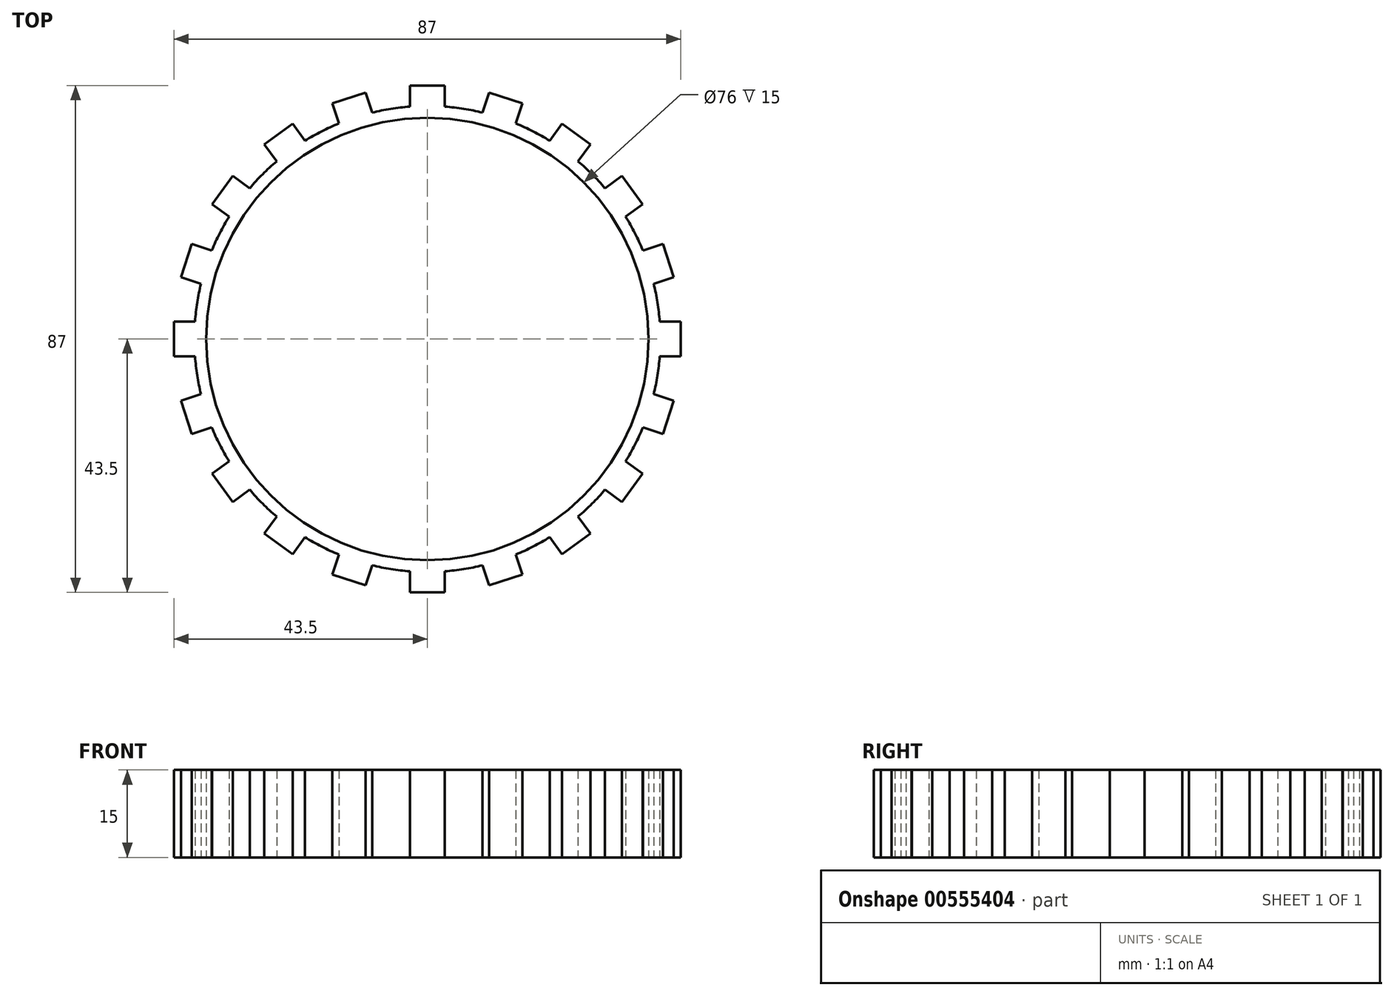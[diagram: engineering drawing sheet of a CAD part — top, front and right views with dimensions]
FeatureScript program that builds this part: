
annotation { "Feature Type Name" : "Feature", "Feature Type Description" : "" }
export const myFeature = defineFeature(function(context is Context, id is Id, definition is map)
    precondition{}
    {
        {
            var Q0;
            Q0=qCreatedBy(makeId("Top.planeOp"),FACE);
            var sketch = newSketch(context, id + "F0", { "sketchPlane" : qUnion([Q0])});
            skCircle(sketch, "E0", {"center": v(0, 0) * mm, "radius": 40 * mm});
            skCircle(sketch, "E1.0", {"center": v(0, 0) * mm, "radius": 38 * mm});
            skPoint(sketch, "E2", {"position": v(0, 41.5) * mm});
            skLineSegment(sketch, "E3.bottom", {"start": v(3, 39.5) * mm, "end": v(-3, 39.5) * mm});
            skLineSegment(sketch, "E3.top", {"start": v(3, 43.5) * mm, "end": v(-3, 43.5) * mm});
            skLineSegment(sketch, "E3.left", {"start": v(3, 39.5) * mm, "end": v(3, 43.5) * mm});
            skLineSegment(sketch, "E3.right", {"start": v(-3, 39.5) * mm, "end": v(-3, 43.5) * mm});
            skLineSegment(sketch, "E4.1.0", {"start": v(-10.59, 42.3) * mm, "end": v(-16.3, 40.44) * mm});
            skLineSegment(sketch, "E4.1.1", {"start": v(-15.06, 36.64) * mm, "end": v(-16.3, 40.44) * mm});
            skLineSegment(sketch, "E4.2.0", {"start": v(-23.14, 36.96) * mm, "end": v(-28, 33.43) * mm});
            skLineSegment(sketch, "E4.2.1", {"start": v(-25.64, 30.2) * mm, "end": v(-28, 33.43) * mm});
            skLineSegment(sketch, "E5.2.3.0", {"start": v(-33.43, 28) * mm, "end": v(-36.96, 23.14) * mm});
            skLineSegment(sketch, "E5.3.3.0", {"start": v(-33.72, 20.8) * mm, "end": v(-36.96, 23.14) * mm});
            skLineSegment(sketch, "E5.2.4.0", {"start": v(-40.44, 16.3) * mm, "end": v(-42.3, 10.59) * mm});
            skLineSegment(sketch, "E5.3.4.0", {"start": v(-38.5, 9.35) * mm, "end": v(-42.3, 10.59) * mm});
            skLineSegment(sketch, "E5.2.5.0", {"start": v(-43.5, 3) * mm, "end": v(-43.5, -3) * mm});
            skLineSegment(sketch, "E5.3.5.0", {"start": v(-39.5, -3) * mm, "end": v(-43.5, -3) * mm});
            skLineSegment(sketch, "E5.2.6.0", {"start": v(-42.3, -10.59) * mm, "end": v(-40.44, -16.3) * mm});
            skLineSegment(sketch, "E5.3.6.0", {"start": v(-36.64, -15.06) * mm, "end": v(-40.44, -16.3) * mm});
            skLineSegment(sketch, "E5.2.7.0", {"start": v(-36.96, -23.14) * mm, "end": v(-33.43, -28) * mm});
            skLineSegment(sketch, "E5.3.7.0", {"start": v(-30.2, -25.64) * mm, "end": v(-33.43, -28) * mm});
            skLineSegment(sketch, "E5.2.8.0", {"start": v(-28, -33.43) * mm, "end": v(-23.14, -36.96) * mm});
            skLineSegment(sketch, "E5.3.8.0", {"start": v(-20.8, -33.72) * mm, "end": v(-23.14, -36.96) * mm});
            skLineSegment(sketch, "E5.2.9.0", {"start": v(-16.3, -40.44) * mm, "end": v(-10.59, -42.3) * mm});
            skLineSegment(sketch, "E5.3.9.0", {"start": v(-9.35, -38.5) * mm, "end": v(-10.59, -42.3) * mm});
            skLineSegment(sketch, "E6.2.10.0", {"start": v(-3, -43.5) * mm, "end": v(3, -43.5) * mm});
            skLineSegment(sketch, "E6.3.10.0", {"start": v(3, -39.5) * mm, "end": v(3, -43.5) * mm});
            skLineSegment(sketch, "E6.2.11.0", {"start": v(10.59, -42.3) * mm, "end": v(16.3, -40.44) * mm});
            skLineSegment(sketch, "E6.3.11.0", {"start": v(15.06, -36.64) * mm, "end": v(16.3, -40.44) * mm});
            skLineSegment(sketch, "E6.2.12.0", {"start": v(23.14, -36.96) * mm, "end": v(28, -33.43) * mm});
            skLineSegment(sketch, "E6.3.12.0", {"start": v(25.64, -30.2) * mm, "end": v(28, -33.43) * mm});
            skLineSegment(sketch, "E6.2.13.0", {"start": v(33.43, -28) * mm, "end": v(36.96, -23.14) * mm});
            skLineSegment(sketch, "E6.3.13.0", {"start": v(33.72, -20.8) * mm, "end": v(36.96, -23.14) * mm});
            skLineSegment(sketch, "E6.2.14.0", {"start": v(40.44, -16.3) * mm, "end": v(42.3, -10.59) * mm});
            skLineSegment(sketch, "E6.3.14.0", {"start": v(38.5, -9.35) * mm, "end": v(42.3, -10.59) * mm});
            skLineSegment(sketch, "E6.2.15.0", {"start": v(43.5, -3) * mm, "end": v(43.5, 3) * mm});
            skLineSegment(sketch, "E6.3.15.0", {"start": v(39.5, 3) * mm, "end": v(43.5, 3) * mm});
            skLineSegment(sketch, "E6.2.16.0", {"start": v(42.3, 10.59) * mm, "end": v(40.44, 16.3) * mm});
            skLineSegment(sketch, "E6.3.16.0", {"start": v(36.64, 15.06) * mm, "end": v(40.44, 16.3) * mm});
            skLineSegment(sketch, "E6.2.17.0", {"start": v(36.96, 23.14) * mm, "end": v(33.43, 28) * mm});
            skLineSegment(sketch, "E6.3.17.0", {"start": v(30.2, 25.64) * mm, "end": v(33.43, 28) * mm});
            skLineSegment(sketch, "E6.2.18.0", {"start": v(28, 33.43) * mm, "end": v(23.14, 36.96) * mm});
            skLineSegment(sketch, "E6.3.18.0", {"start": v(20.8, 33.72) * mm, "end": v(23.14, 36.96) * mm});
            skLineSegment(sketch, "E6.2.19.0", {"start": v(16.3, 40.44) * mm, "end": v(10.59, 42.3) * mm});
            skLineSegment(sketch, "E6.3.19.0", {"start": v(9.35, 38.5) * mm, "end": v(10.59, 42.3) * mm});
            skLineSegment(sketch, "E7.1.0", {"start": v(-9.35, 38.5) * mm, "end": v(-10.59, 42.3) * mm});
            skPoint(sketch, "E7.1.1", {"position": v(-12.82, 39.47) * mm});
            skLineSegment(sketch, "E7.1.2", {"start": v(-9.35, 38.5) * mm, "end": v(-15.06, 36.64) * mm});
            skPoint(sketch, "E7.1.5", {"position": v(-12.82, 39.47) * mm});
            skLineSegment(sketch, "E7.2.0", {"start": v(-20.8, 33.72) * mm, "end": v(-23.14, 36.96) * mm});
            skPoint(sketch, "E7.2.1", {"position": v(-24.4, 33.57) * mm});
            skLineSegment(sketch, "E7.2.2", {"start": v(-20.8, 33.72) * mm, "end": v(-25.64, 30.2) * mm});
            skPoint(sketch, "E7.2.5", {"position": v(-24.4, 33.57) * mm});
            skLineSegment(sketch, "E7.3.0", {"start": v(-30.2, 25.64) * mm, "end": v(-33.43, 28) * mm});
            skPoint(sketch, "E7.3.1", {"position": v(-33.57, 24.4) * mm});
            skLineSegment(sketch, "E7.3.2", {"start": v(-30.2, 25.64) * mm, "end": v(-33.72, 20.8) * mm});
            skPoint(sketch, "E7.3.5", {"position": v(-33.57, 24.4) * mm});
            skLineSegment(sketch, "E7.4.0", {"start": v(-36.64, 15.06) * mm, "end": v(-40.44, 16.3) * mm});
            skPoint(sketch, "E7.4.1", {"position": v(-39.47, 12.82) * mm});
            skLineSegment(sketch, "E7.4.2", {"start": v(-36.64, 15.06) * mm, "end": v(-38.5, 9.35) * mm});
            skPoint(sketch, "E7.4.5", {"position": v(-39.47, 12.82) * mm});
            skLineSegment(sketch, "E7.5.0", {"start": v(-39.5, 3) * mm, "end": v(-43.5, 3) * mm});
            skPoint(sketch, "E7.5.1", {"position": v(-41.5, 0) * mm});
            skLineSegment(sketch, "E7.5.2", {"start": v(-39.5, 3) * mm, "end": v(-39.5, -3) * mm});
            skPoint(sketch, "E7.5.5", {"position": v(-41.5, 0) * mm});
            skLineSegment(sketch, "E7.6.0", {"start": v(-38.5, -9.35) * mm, "end": v(-42.3, -10.59) * mm});
            skPoint(sketch, "E7.6.1", {"position": v(-39.47, -12.82) * mm});
            skLineSegment(sketch, "E7.6.2", {"start": v(-38.5, -9.35) * mm, "end": v(-36.64, -15.06) * mm});
            skPoint(sketch, "E7.6.5", {"position": v(-39.47, -12.82) * mm});
            skLineSegment(sketch, "E7.7.0", {"start": v(-33.72, -20.8) * mm, "end": v(-36.96, -23.14) * mm});
            skPoint(sketch, "E7.7.1", {"position": v(-33.57, -24.4) * mm});
            skLineSegment(sketch, "E7.7.2", {"start": v(-33.72, -20.8) * mm, "end": v(-30.2, -25.64) * mm});
            skPoint(sketch, "E7.7.5", {"position": v(-33.57, -24.4) * mm});
            skLineSegment(sketch, "E7.8.0", {"start": v(-25.64, -30.2) * mm, "end": v(-28, -33.43) * mm});
            skPoint(sketch, "E7.8.1", {"position": v(-24.4, -33.57) * mm});
            skLineSegment(sketch, "E7.8.2", {"start": v(-25.64, -30.2) * mm, "end": v(-20.8, -33.72) * mm});
            skPoint(sketch, "E7.8.5", {"position": v(-24.4, -33.57) * mm});
            skLineSegment(sketch, "E7.9.0", {"start": v(-15.06, -36.64) * mm, "end": v(-16.3, -40.44) * mm});
            skPoint(sketch, "E7.9.1", {"position": v(-12.82, -39.47) * mm});
            skLineSegment(sketch, "E7.9.2", {"start": v(-15.06, -36.64) * mm, "end": v(-9.35, -38.5) * mm});
            skPoint(sketch, "E7.9.5", {"position": v(-12.82, -39.47) * mm});
            skLineSegment(sketch, "E7.10.0", {"start": v(-3, -39.5) * mm, "end": v(-3, -43.5) * mm});
            skPoint(sketch, "E7.10.1", {"position": v(0, -41.5) * mm});
            skLineSegment(sketch, "E7.10.2", {"start": v(-3, -39.5) * mm, "end": v(3, -39.5) * mm});
            skPoint(sketch, "E7.10.5", {"position": v(0, -41.5) * mm});
            skLineSegment(sketch, "E7.11.0", {"start": v(9.35, -38.5) * mm, "end": v(10.59, -42.3) * mm});
            skPoint(sketch, "E7.11.1", {"position": v(12.82, -39.47) * mm});
            skLineSegment(sketch, "E7.11.2", {"start": v(9.35, -38.5) * mm, "end": v(15.06, -36.64) * mm});
            skPoint(sketch, "E7.11.5", {"position": v(12.82, -39.47) * mm});
            skLineSegment(sketch, "E7.12.0", {"start": v(20.8, -33.72) * mm, "end": v(23.14, -36.96) * mm});
            skPoint(sketch, "E7.12.1", {"position": v(24.4, -33.57) * mm});
            skLineSegment(sketch, "E7.12.2", {"start": v(20.8, -33.72) * mm, "end": v(25.64, -30.2) * mm});
            skPoint(sketch, "E7.12.5", {"position": v(24.4, -33.57) * mm});
            skLineSegment(sketch, "E7.13.0", {"start": v(30.2, -25.64) * mm, "end": v(33.43, -28) * mm});
            skPoint(sketch, "E7.13.1", {"position": v(33.57, -24.4) * mm});
            skLineSegment(sketch, "E7.13.2", {"start": v(30.2, -25.64) * mm, "end": v(33.72, -20.8) * mm});
            skPoint(sketch, "E7.13.5", {"position": v(33.57, -24.4) * mm});
            skLineSegment(sketch, "E7.14.0", {"start": v(36.64, -15.06) * mm, "end": v(40.44, -16.3) * mm});
            skPoint(sketch, "E7.14.1", {"position": v(39.47, -12.82) * mm});
            skLineSegment(sketch, "E7.14.2", {"start": v(36.64, -15.06) * mm, "end": v(38.5, -9.35) * mm});
            skPoint(sketch, "E7.14.5", {"position": v(39.47, -12.82) * mm});
            skLineSegment(sketch, "E7.15.0", {"start": v(39.5, -3) * mm, "end": v(43.5, -3) * mm});
            skPoint(sketch, "E7.15.1", {"position": v(41.5, 0) * mm});
            skLineSegment(sketch, "E7.15.2", {"start": v(39.5, -3) * mm, "end": v(39.5, 3) * mm});
            skPoint(sketch, "E7.15.5", {"position": v(41.5, 0) * mm});
            skLineSegment(sketch, "E7.16.0", {"start": v(38.5, 9.35) * mm, "end": v(42.3, 10.59) * mm});
            skPoint(sketch, "E7.16.1", {"position": v(39.47, 12.82) * mm});
            skLineSegment(sketch, "E7.16.2", {"start": v(38.5, 9.35) * mm, "end": v(36.64, 15.06) * mm});
            skPoint(sketch, "E7.16.5", {"position": v(39.47, 12.82) * mm});
            skLineSegment(sketch, "E7.17.0", {"start": v(33.72, 20.8) * mm, "end": v(36.96, 23.14) * mm});
            skPoint(sketch, "E7.17.1", {"position": v(33.57, 24.4) * mm});
            skLineSegment(sketch, "E7.17.2", {"start": v(33.72, 20.8) * mm, "end": v(30.2, 25.64) * mm});
            skPoint(sketch, "E7.17.5", {"position": v(33.57, 24.4) * mm});
            skLineSegment(sketch, "E7.18.0", {"start": v(25.64, 30.2) * mm, "end": v(28, 33.43) * mm});
            skPoint(sketch, "E7.18.1", {"position": v(24.4, 33.57) * mm});
            skLineSegment(sketch, "E7.18.2", {"start": v(25.64, 30.2) * mm, "end": v(20.8, 33.72) * mm});
            skPoint(sketch, "E7.18.5", {"position": v(24.4, 33.57) * mm});
            skLineSegment(sketch, "E7.19.0", {"start": v(15.06, 36.64) * mm, "end": v(16.3, 40.44) * mm});
            skPoint(sketch, "E7.19.1", {"position": v(12.82, 39.47) * mm});
            skLineSegment(sketch, "E7.19.2", {"start": v(15.06, 36.64) * mm, "end": v(9.35, 38.5) * mm});
            skPoint(sketch, "E7.19.5", {"position": v(12.82, 39.47) * mm});
            skSolve(sketch);
        }
        {
            var Q0;
            Q0 = qSketchRegion(id + "F0", true);
            extrude(context, id + "F1", {"entities" : qUnion([Q0]), "depth" : 15 * mm, "offsetDistance" : 25 * mm});
        }
    });
